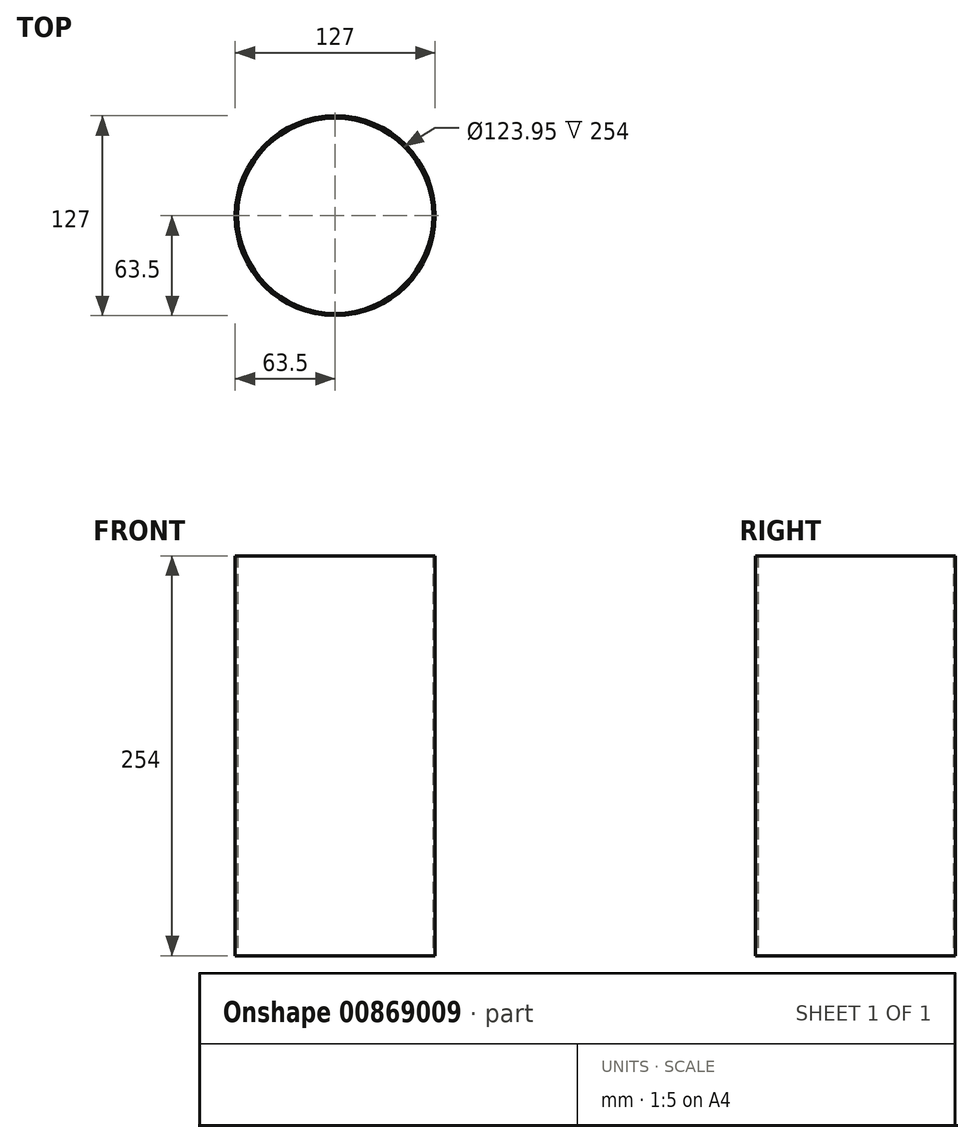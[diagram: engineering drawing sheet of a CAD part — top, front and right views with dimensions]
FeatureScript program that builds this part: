
annotation { "Feature Type Name" : "Feature", "Feature Type Description" : "" }
export const myFeature = defineFeature(function(context is Context, id is Id, definition is map)
    precondition{}
    {
        {
            var Q0;
            Q0=qCreatedBy(makeId("Top.planeOp"),FACE);
            var sketch = newSketch(context, id + "F0", { "sketchPlane" : qUnion([Q0])});
            skCircle(sketch, "E0", {"center": v(0, 0) * mm, "radius": 63.5 * mm});
            skCircle(sketch, "E1.0", {"center": v(0, 0) * mm, "radius": 61.98 * mm});
            skSolve(sketch);
        }
        {
            var Q0;
            Q0=qSketchRegion(id+"F0",true);
            extrude(context, id + "F1", {"entities" : qUnion([Q0]), "depth" : 254 * mm, "offsetDistance" : 25.4 * mm});
        }
    });
